# Revit family: 6kt.Mutter FK 10, M12, ZnNi
name_source: partatom
category: HLS-Bauteile
revit_build: Autodesk Revit 2017 (Build: 20190507_1515(x64)
units: mm (PartAtom-declared; Revit-internal decimal feet)

## family parameters
Arbeitsebenenbasiert = Ja
Beim Laden mit Abzugskörper schneiden = Nein
Bemaßung runder Anschluss = Durchmesser verwenden
Gemeinsam genutzt = Ja
Immer vertikal = Nein
Raumberechnungspunkt = Nein
Teiletyp = Normal

## types (1)
- 6kt.Mutter M12, FK 10, ZnNi
    Artikelnummer = 8989995/zn
    EAN = 4250928448439
    F2 = 9 mm  [stored 0.0295276 ft]
    Fabrikat = MEFA
    Firma = MEFA Befestigungs- und Montagesysteme GmbH
    Gewicht = 0.02 kg
    Gewicht pro Bauteil = 0.02 kg
    Gewinde = M12
    H = 10 mm  [stored 0.0328084 ft]
    Kurztext1 = Sechskantmutter Stahl FK 10 ZnNi
    Kurztext2 = M12 SW 19
    Lochung = 5 mm  [stored 0.0164042 ft]
    Material = Stahl
    Mengeneinheit = St
    Oberflaeche = Zink-Nickel
    Schlüsselweite = 19
    Vorgabe-Ansicht = 1219 mm
    vpe = 100 St

note: [stored X ft] marks values corroborated as IEEE doubles in the binary element streams (Revit-internal decimal feet)

## geometry (parser evidence)
native form markers: Sweep x3
no freeform markers — native parametric forms only
